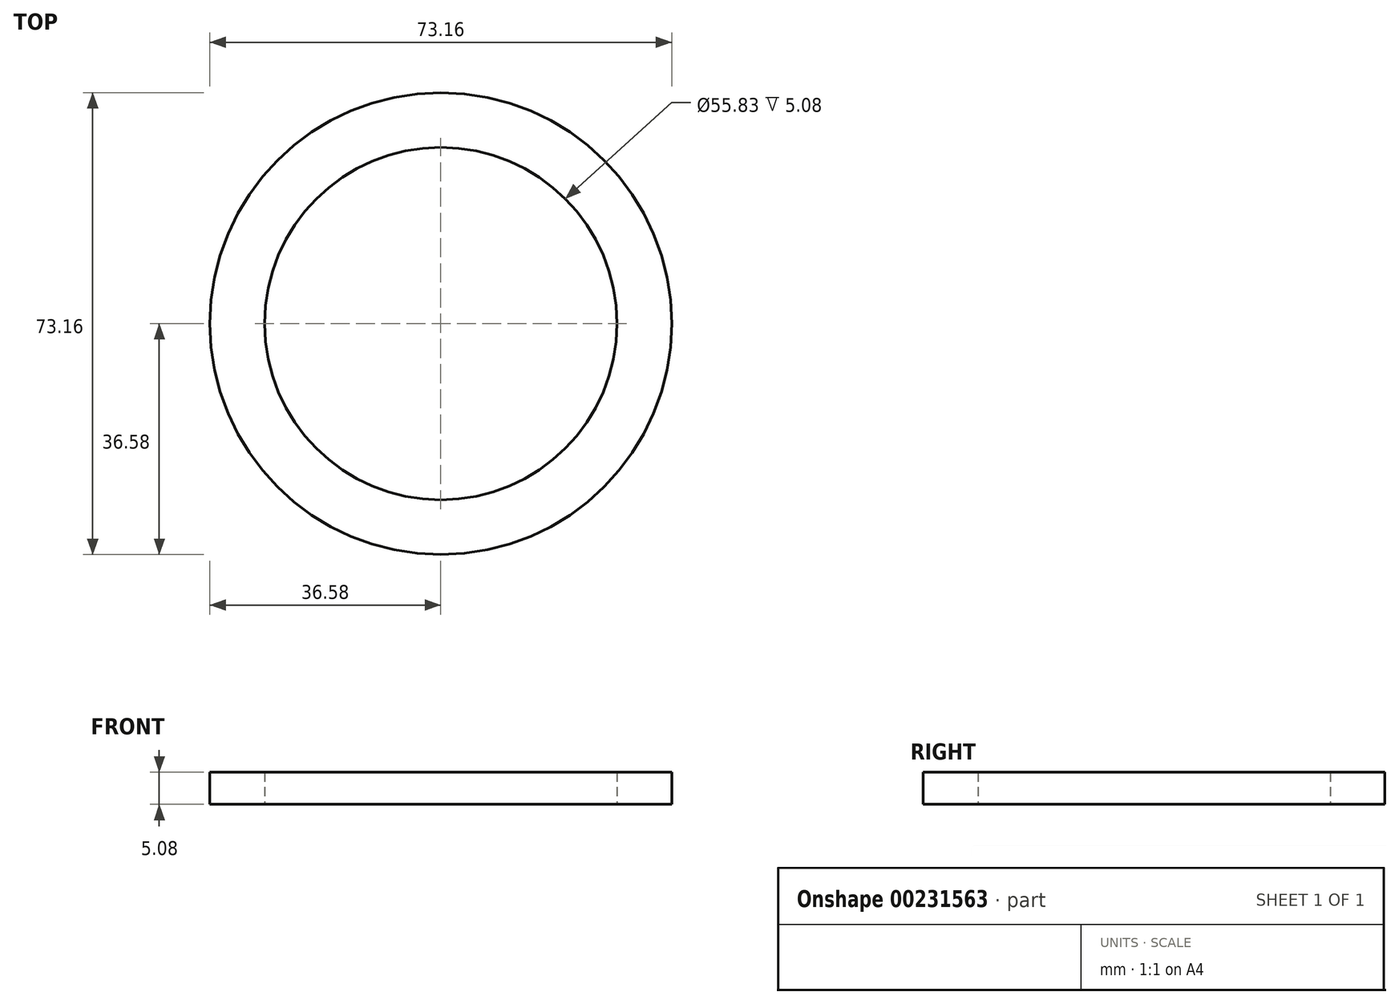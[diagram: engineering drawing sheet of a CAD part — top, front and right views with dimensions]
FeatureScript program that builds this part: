
annotation { "Feature Type Name" : "Feature", "Feature Type Description" : "" }
export const myFeature = defineFeature(function(context is Context, id is Id, definition is map)
    precondition{}
    {
        {
            var Q0;
            Q0=qCreatedBy(makeId("Top.planeOp"),FACE);
            var sketch = newSketch(context, id + "F0", { "sketchPlane" : qUnion([Q0])});
            skCircle(sketch, "E0", {"center": v(0, 0) * mm, "radius": 27.92 * mm});
            skCircle(sketch, "E1", {"center": v(0, 0) * mm, "radius": 36.58 * mm});
            skSolve(sketch);
        }
        {
            var Q0;
            Q0 = qSketchRegion(id + "F0", true);
            extrude(context, id + "F1", {"entities" : qUnion([Q0]), "depth" : 5.08 * mm});
        }
    });
